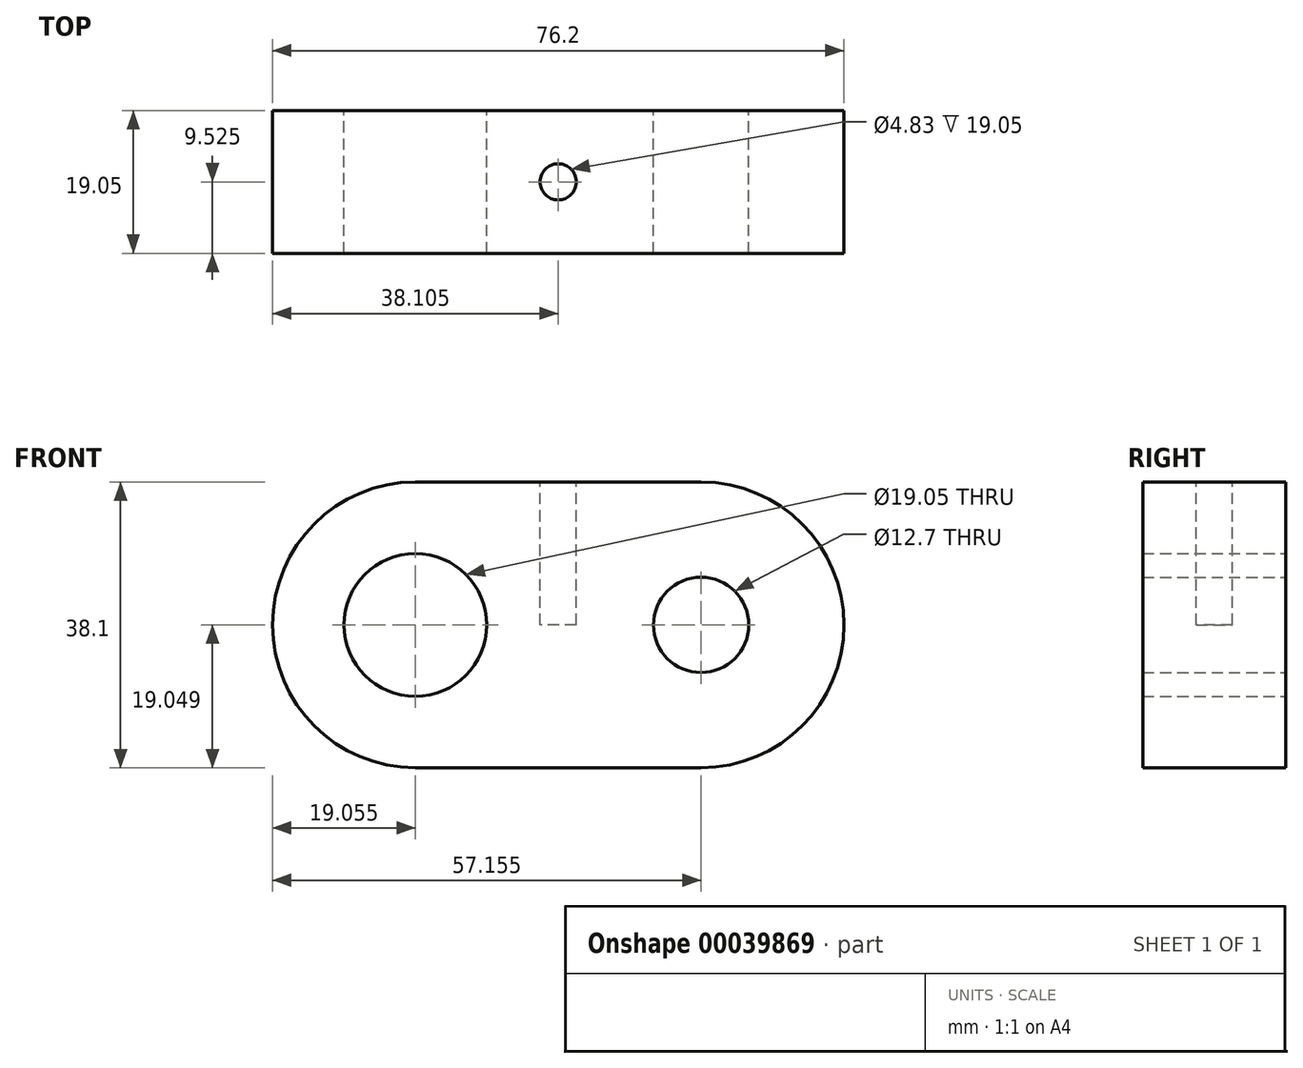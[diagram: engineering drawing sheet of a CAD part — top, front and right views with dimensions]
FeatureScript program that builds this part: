
annotation { "Feature Type Name" : "Feature", "Feature Type Description" : "" }
export const myFeature = defineFeature(function(context is Context, id is Id, definition is map)
    precondition{}
    {
        {
            var Q0;
            Q0=qCreatedBy(makeId("Front.planeOp"),FACE);
            var sketch = newSketch(context, id + "F0", { "sketchPlane" : qUnion([Q0])});
            skLineSegment(sketch, "E0.bottom", {"start": v(-43.54, 33) * mm, "end": v(-5.44, 33) * mm});
            skLineSegment(sketch, "E0.top", {"start": v(-43.54, -5.1) * mm, "end": v(-5.44, -5.1) * mm});
            skLineSegment(sketch, "E0.left", {"start": v(-62.59, 13.95) * mm, "end": v(-62.59, 13.95) * mm});
            skLineSegment(sketch, "E0.right", {"start": v(13.61, 13.95) * mm, "end": v(13.61, 13.95) * mm});
            skPoint(sketch, "E1.visualSharp", {"position": v(-62.59, 33) * mm});
            skArc(sketch, "E1.filletArc", {"start": v(-43.54, 33) * mm, "mid": v(-57, 27.42) * mm, "end": v(-62.59, 13.95) * mm});
            skPoint(sketch, "E2.visualSharp", {"position": v(13.61, 33) * mm});
            skArc(sketch, "E2.filletArc", {"start": v(13.61, 13.95) * mm, "mid": v(8.04, 27.42) * mm, "end": v(-5.44, 33) * mm});
            skPoint(sketch, "E3.visualSharp", {"position": v(-62.59, -5.1) * mm});
            skArc(sketch, "E3.filletArc", {"start": v(-62.59, 13.95) * mm, "mid": v(-57, 0.48) * mm, "end": v(-43.54, -5.1) * mm});
            skPoint(sketch, "E4.visualSharp", {"position": v(13.61, -5.1) * mm});
            skArc(sketch, "E4.filletArc", {"start": v(-5.44, -5.1) * mm, "mid": v(8.04, 0.48) * mm, "end": v(13.61, 13.95) * mm});
            skCircle(sketch, "E5", {"center": v(-43.54, 13.95) * mm, "radius": 9.53 * mm});
            skCircle(sketch, "E6", {"center": v(-5.44, 13.95) * mm, "radius": 6.35 * mm});
            skSolve(sketch);
        }
        {
            var Q0;
            Q0=makeQuery(id+"F0.imprint","IMPRINT",FACE,{"disambiguationData":[TD([[makeQuery(id+"F0.imprint","IMPRINT",EDGE,{"derivedFrom":sQuery(id+"F0.wireOp",EDGE,"E0.bottom")}),-1.0]])]});
            extrude(context, id + "F1", {"entities" : qUnion([Q0]), "depth" : 19.05 * mm});
        }
        {
            var Q0;
            Q0=makeQuery(id+"F1.opExtrude","SWEPT_FACE",FACE,{"disambiguationData":[OSD([sQuery(id+"F0.wireOp",EDGE,"E0.bottom")])]});
            var sketch = newSketch(context, id + "F2", { "sketchPlane" : qUnion([Q0])});
            skLineSegment(sketch, "E7", {"start": v(-62.59, -19.05) * mm, "end": v(-62.59, 0) * mm});
            skLineSegment(sketch, "E8", {"start": v(13.61, 0) * mm, "end": v(13.61, -19.05) * mm});
            skCircle(sketch, "E9", {"center": v(-24.49, -9.53) * mm, "radius": 2.41 * mm});
            skPoint(sketch, "E9.centerSnap0", {"position": v(-24.49, 0) * mm});
            skSolve(sketch);
        }
        {
            var Q0;
            Q0 = qSketchRegion(id + "F2", true);
            extrude(context, id + "F3", {"entities" : qUnion([Q0]), "operationType" : NewBodyOperationType.REMOVE, "oppositeDirection" : true, "depth" : 19.05 * mm});
        }
    });
